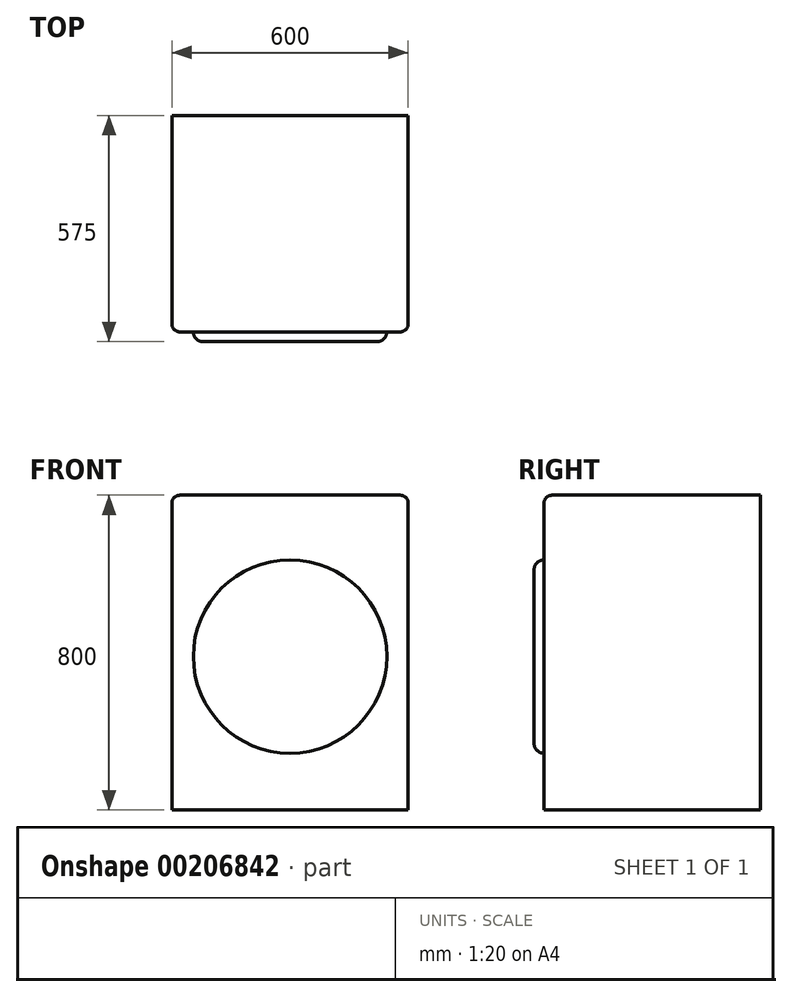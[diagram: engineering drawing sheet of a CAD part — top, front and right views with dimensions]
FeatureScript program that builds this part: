
annotation { "Feature Type Name" : "Feature", "Feature Type Description" : "" }
export const myFeature = defineFeature(function(context is Context, id is Id, definition is map)
    precondition{}
    {
        {
            var Q0;
            Q0=qCreatedBy(makeId("Top.planeOp"),FACE);
            var sketch = newSketch(context, id + "F0", { "sketchPlane" : qUnion([Q0])});
            skLineSegment(sketch, "E0.bottom", {"start": v(-518.83, 504.1) * mm, "end": v(81.17, 504.1) * mm});
            skLineSegment(sketch, "E0.top", {"start": v(-518.83, -45.9) * mm, "end": v(-500.83, -45.9) * mm});
            skLineSegment(sketch, "E0.left", {"start": v(-518.83, 504.1) * mm, "end": v(-518.83, -45.9) * mm});
            skLineSegment(sketch, "E0.right", {"start": v(81.17, 504.1) * mm, "end": v(81.17, -45.9) * mm});
            skLineSegment(sketch, "E1.bottom", {"start": v(-500.83, 501.1) * mm, "end": v(63.17, 501.1) * mm});
            skLineSegment(sketch, "E1.left", {"start": v(-500.83, 501.1) * mm, "end": v(-500.83, -45.9) * mm});
            skLineSegment(sketch, "E1.right", {"start": v(63.17, 501.1) * mm, "end": v(63.17, -45.9) * mm});
            skLineSegment(sketch, "E2.trimOffspring", {"start": v(63.17, -45.9) * mm, "end": v(81.17, -45.9) * mm});
            skSolve(sketch);
        }
        {
            var Q0;
            Q0=qCreatedBy(makeId("Top.planeOp"),FACE);
            var sketch = newSketch(context, id + "F1", { "sketchPlane" : qUnion([Q0])});
            skPoint(sketch, "E3.0", {"position": v(-518.83, 504.1) * mm});
            skLineSegment(sketch, "E4.0", {"start": v(-518.83, 504.1) * mm, "end": v(-518.83, -45.9) * mm});
            skLineSegment(sketch, "E5.0", {"start": v(-518.83, 504.1) * mm, "end": v(81.17, 504.1) * mm});
            skLineSegment(sketch, "E6.0", {"start": v(81.17, 504.1) * mm, "end": v(81.17, -45.9) * mm});
            skLineSegment(sketch, "E7", {"start": v(-518.83, -45.9) * mm, "end": v(81.17, -45.9) * mm});
            skSolve(sketch);
        }
        {
            var Q0;
            Q0=qSketchRegion(id+"F0",true);
            extrude(context, id + "F2", {"entities" : qUnion([Q0]), "depth" : 700 * mm});
        }
        {
            var Q0;
            Q0=qSketchRegion(id+"F1",true);
            extrude(context, id + "F3", {"entities" : qUnion([Q0]), "operationType" : NewBodyOperationType.ADD, "depth" : 800 * mm});
        }
        {
            var Q0;
            Q0=makeQuery(id+"F3.opExtrude","CAP_EDGE",EDGE,{"disambiguationData":[OSD([sQuery(id+"F1.wireOp",EDGE,"E7")])],"isStart":false});
            var Q1;
            Q1=makeQuery(id+"F3.opExtrude","CAP_EDGE",EDGE,{"disambiguationData":[OSD([sQuery(id+"F1.wireOp",EDGE,"E6.0")])],"isStart":false});
            var Q2;
            Q2=makeQuery(id+"F3.opExtrude","CAP_EDGE",EDGE,{"disambiguationData":[OSD([sQuery(id+"F1.wireOp",EDGE,"E4.0")])],"isStart":false});
            var Q3;
            Q3=makeQuery(id+"F3.boolean.opBoolean","MERGE",EDGE,{"derivedFrom":[makeQuery(id+"F2.opExtrude","SWEPT_EDGE",EDGE,{"disambiguationData":[OSD([sQuery(id+"F0.wireOp",EDGE,"E0.right"),sQuery(id+"F0.wireOp",EDGE,"E2.trimOffspring")])]}),makeQuery(id+"F3.opExtrude","SWEPT_EDGE",EDGE,{"disambiguationData":[OSD([sQuery(id+"F1.wireOp",EDGE,"E6.0"),sQuery(id+"F1.wireOp",EDGE,"E7")])]})]});
            var Q4;
            Q4=makeQuery(id+"F3.boolean.opBoolean","MERGE",EDGE,{"derivedFrom":[makeQuery(id+"F2.opExtrude","SWEPT_EDGE",EDGE,{"disambiguationData":[OSD([sQuery(id+"F0.wireOp",EDGE,"E0.top"),sQuery(id+"F0.wireOp",EDGE,"E0.left")])]}),makeQuery(id+"F3.opExtrude","SWEPT_EDGE",EDGE,{"disambiguationData":[OSD([sQuery(id+"F1.wireOp",EDGE,"E4.0"),sQuery(id+"F1.wireOp",EDGE,"E7")])]})]});
            fillet(context, id + "F4", {"entities" : qUnion([Q0, Q1, Q2, Q3, Q4]), "radius" : 20 * mm, "tangentPropagation" : true, "allowEdgeOverflow" : false});
        }
        {
            var Q0;
            Q0=makeQuery(id+"F3.boolean.opBoolean","MERGE",FACE,{"derivedFrom":[makeQuery(id+"F2.opExtrude","SWEPT_FACE",FACE,{"disambiguationData":[OSD([sQuery(id+"F0.wireOp",EDGE,"E0.top")])]}),makeQuery(id+"F2.opExtrude","SWEPT_FACE",FACE,{"disambiguationData":[OSD([sQuery(id+"F0.wireOp",EDGE,"E2.trimOffspring")])]}),makeQuery(id+"F3.opExtrude","SWEPT_FACE",FACE,{"disambiguationData":[OSD([sQuery(id+"F1.wireOp",EDGE,"E7")])]})]});
            var sketch = newSketch(context, id + "F5", { "sketchPlane" : qUnion([Q0])});
            skCircle(sketch, "E8", {"center": v(-218.83, 390) * mm, "radius": 245.7 * mm});
            skPoint(sketch, "E8.centerSnap0", {"position": v(-498.83, 390) * mm});
            skPoint(sketch, "E8.centerSnap1", {"position": v(-218.83, 780) * mm});
            skSolve(sketch);
        }
        {
            var Q0;
            Q0 = qSketchRegion(id + "F5", true);
            extrude(context, id + "F6", {"entities" : qUnion([Q0]), "operationType" : NewBodyOperationType.ADD, "depth" : 25 * mm});
        }
        {
            var Q0;
            Q0=makeQuery(id+"F6.opExtrude","CAP_EDGE",EDGE,{"disambiguationData":[OSD([sQuery(id+"F5.wireOp",EDGE,"E8")])],"isStart":false});
            fillet(context, id + "F7", {"entities" : qUnion([Q0]), "radius" : 25 * mm, "tangentPropagation" : true, "allowEdgeOverflow" : false});
        }
    });
